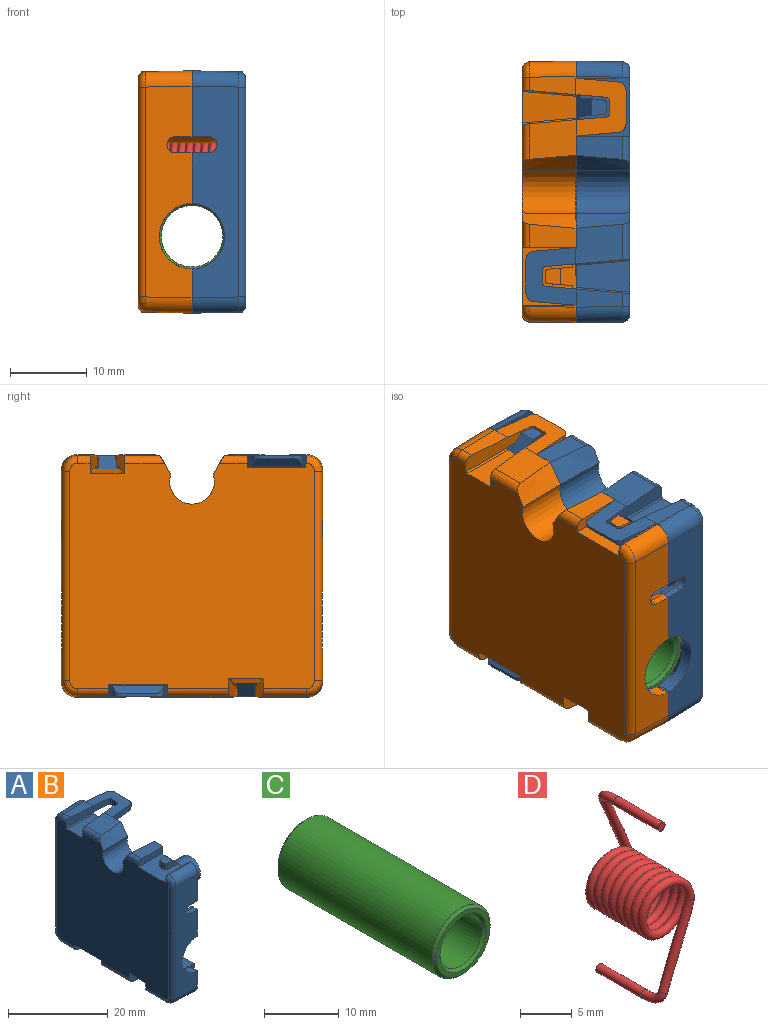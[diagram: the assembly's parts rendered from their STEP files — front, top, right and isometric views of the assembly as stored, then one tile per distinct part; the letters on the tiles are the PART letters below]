
ASSEMBLY  parts=4 mates=3
PART A: 258 faces, bbox 13.6x34.1x31.6 mm
  f0: torus R=1.84mm, axis (1,0,0), area 7.5mm2, adj f8,f153
  f1: torus R=1.85mm, axis (1,0,0), area 7.5mm2, adj f11,f71
  f2: torus R=0.75mm, axis (1,0,0), area 5.3mm2, adj f8,f70
  f3: cylinder r=4.25mm len=8.49mm, axis (0,1,0), area 22.1mm2, adj f118,f119,f120,f121,f138,f139,f140,f163
  f4: cylinder r=4.25mm len=8.49mm, axis (0,1,0), area 22.1mm2, adj f111,f113,f115,f116,f124,f136,f137,f158
  f5: cone r=2.9mm half-angle=0.5deg, axis (1,0,0), area 77.5mm2, adj f46,f125,f126,f228
  f6: torus R=2.54mm, axis (1,0,0), area 10.9mm2, adj f10,f153
  f7: cylinder r=5.7mm len=30mm, axis (0,1,0), area 113.7mm2, adj f18,f19,f20,f21,f22,f23,f24,f25
  f8: cone r=1.25mm half-angle=0.5deg, axis (-1,0,0), area 77.4mm2, adj f0,f2
  f9: cone r=2.85mm half-angle=0.5deg, axis (-1,0,0), area 191.1mm2, adj f71,f153
  f10: cone r=2mm half-angle=0.5deg, axis (-1,0,0), area 63.6mm2, adj f6,f69
  f11: cone r=1.35mm half-angle=0.5deg, axis (1,0,0), area 81.8mm2, adj f1,f52
  f12: cone r=1mm half-angle=0.5deg, axis (1,0,0), area 33.7mm2, adj f69,f170
  f13: bspline ~1.09x0.98mm, area 0.8mm2, adj f159,f171,f173,f204
  f14: bspline ~1.09x0.98mm, area 0.8mm2, adj f15,f156,f172,f219
  f15: cylinder r=1mm len=1mm, axis (0,1,0), area 1.5mm2, adj f14,f207,f219,f220
  f16: cylinder r=1mm len=1.52mm, axis (0,1,0), area 2.3mm2, adj f159,f203,f204,f206
  f17: cylinder r=1mm len=1.52mm, axis (0,1,0), area 2.3mm2, adj f156,f207,f218,f219
  f18: plane 2.5x0.33mm, normal (0.01,0,-1), area 0.8mm2, adj f7,f20,f21,f132
  f19: plane 2.5x0.33mm, normal (0.01,0,1), area 0.8mm2, adj f7,f20,f21,f132
  f20: plane 1x0.35mm, normal (0.01,-1,0), area 0.3mm2, adj f7,f18,f19,f132
  f21: plane 1x0.35mm, normal (0.01,1,0), area 0.3mm2, adj f7,f18,f19,f132
  f22: plane 1x0.35mm, normal (0.01,1,0), area 0.3mm2, adj f7,f23,f25,f134
  f23: plane 2.5x0.33mm, normal (0.01,0,-1), area 0.8mm2, adj f7,f22,f24,f134
  f24: plane 1x0.35mm, normal (0.01,-1,0), area 0.3mm2, adj f7,f23,f25,f134
  f25: plane 2.5x0.33mm, normal (0.01,0,1), area 0.8mm2, adj f7,f22,f24,f134
  f26: plane 1x0.35mm, normal (0.01,1,0), area 0.3mm2, adj f7,f27,f28,f135
  f27: plane 2.5x0.33mm, normal (0.01,0,-1), area 0.8mm2, adj f7,f26,f29,f135
  f28: plane 2.5x0.33mm, normal (0.01,0,1), area 0.8mm2, adj f7,f26,f29,f135
  f29: plane 1x0.35mm, normal (0.01,-1,0), area 0.3mm2, adj f7,f27,f28,f135
  f30: plane 3x0.2mm, normal (0.01,1,0), area 0.4mm2, adj f7,f151,f153,f167
  f31: plane 3x0.2mm, normal (0.01,-1,0), area 0.4mm2, adj f7,f152,f153,f165
  f32: plane 1x0.35mm, normal (0.01,-1,0), area 0.3mm2, adj f7,f33,f35,f133
  f33: plane 2.5x0.33mm, normal (0.01,0,1), area 0.8mm2, adj f7,f32,f34,f133
  f34: plane 1x0.35mm, normal (0.01,1,0), area 0.3mm2, adj f7,f33,f35,f133
  f35: plane 2.5x0.33mm, normal (0.01,0,-1), area 0.8mm2, adj f7,f32,f34,f133
  f36: plane 7.01x5.51mm, normal (0.01,1,0), area 21.8mm2, adj f7,f142,f150,f152,f195
  f37: plane 5.51x5.41mm, normal (0.01,-1,0), area 13.1mm2, adj f7,f142,f150,f160,f196
  f38: plane 5.51x5.51mm, normal (0.01,1,0), area 12.4mm2, adj f7,f141,f160,f221,f257
  f39: plane 5.51x5.51mm, normal (0.01,-1,0), area 12.4mm2, adj f7,f141,f167,f186,f257
  f40: plane 5.56x5.51mm, normal (0.01,1,0), area 13.9mm2, adj f7,f41,f143,f153,f223
  f41: plane 5.5x1.6mm, normal (0.01,0,1), area 8.5mm2, adj f40,f42,f153,f223
  f42: plane 5.56x5.51mm, normal (0.01,-1,0), area 13.9mm2, adj f7,f41,f143,f153,f223
  f43: plane 5.56x5.51mm, normal (0.01,-1,0), area 13.9mm2, adj f7,f44,f144,f153,f222
  f44: plane 5.5x1.6mm, normal (0.01,0,1), area 8.5mm2, adj f43,f45,f153,f222
  f45: plane 5.56x5.51mm, normal (0.01,1,0), area 13.9mm2, adj f7,f44,f144,f153,f222
  f46: plane 31.8x29.3mm, normal (-1,0,0), area 881.9mm2, adj f5,f47,f76,f77,f86,f88,f99,f100
  f47: bspline ~2x2mm, area 4mm2, adj f46,f107,f238,f239
  f48: cone r=4.2mm half-angle=1deg, axis (-1,0,0), area 30.9mm2, adj f153,f226,f228,f241
  f49: bspline ~5.58x0.64mm, area 4.3mm2, adj f50,f153,f228,f256
  f50: bspline ~5.5x0.29mm, area 1.6mm2, adj f49,f123,f153,f228
  f51: bspline ~5.5x0.29mm, area 1.6mm2, adj f123,f153,f228,f241
  f52: plane 2.52x2.52mm, normal (1,0,0), area 5mm2, adj f11
  f53: plane 4.08x3.5mm, normal (1,0,0), area 7.8mm2, adj f54,f55,f56,f57,f58,f59,f60,f61
  f54: plane 0.64x0.2mm, normal (0,0,-1), area 0.1mm2, adj f53,f55,f66,f153
  f55: plane 2.21x0.37mm, normal (0,0.99,-0.17), area 0.4mm2, adj f53,f54,f56,f153
  f56: plane 2.21x0.72mm, normal (0,-0.95,-0.31), area 0.5mm2, adj f53,f55,f57,f153
  f57: plane 0.61x0.2mm, normal (0,0,-1), area 0.1mm2, adj f53,f56,f58,f153
  f58: plane 2.21x0.73mm, normal (0,0.95,-0.31), area 0.5mm2, adj f53,f57,f59,f153
  f59: plane 2.21x0.37mm, normal (0,-0.99,-0.17), area 0.4mm2, adj f53,f58,f60,f153
  f60: plane 0.64x0.2mm, normal (0,0,-1), area 0.1mm2, adj f53,f59,f61,f153
  f61: plane 3.5x0.59mm, normal (0,0.99,0.17), area 0.7mm2, adj f53,f60,f62,f153
  f62: plane 0.65x0.2mm, normal (0,0,1), area 0.1mm2, adj f53,f61,f63,f153
  f63: plane 2.44x0.8mm, normal (0,-0.95,0.31), area 0.5mm2, adj f53,f62,f64,f153
  f64: plane 2.44x0.8mm, normal (0,0.95,0.31), area 0.5mm2, adj f53,f63,f65,f153
  f65: plane 0.65x0.2mm, normal (0,0,1), area 0.1mm2, adj f53,f64,f66,f153
  f66: plane 3.5x0.59mm, normal (0,-0.99,0.17), area 0.7mm2, adj f53,f54,f65,f153
  f67: plane 5.5x0.74mm, normal (0.01,0.8,-0.6), area 4.5mm2, adj f153,f191,f226,f228
  f68: plane 5.5x0.74mm, normal (0.01,-0.8,-0.6), area 4.5mm2, adj f153,f224,f225,f228
  f69: plane 4x4mm, normal (1,0,0), area 9.4mm2, adj f10,f12
  f70: plane 1.51x1.51mm, normal (1,0,0), area 1.8mm2, adj f2
  f71: plane 5.7x5.7mm, normal (1,0,0), area 14.8mm2, adj f1,f9
  f72: plane 5.5x0.49mm, normal (0.02,-1,0), area 2.2mm2, adj f73,f153,f173,f210
  f73: plane 5.5x1.1mm, normal (0.02,0,-1), area 5.5mm2, adj f72,f153,f155,f210
  f74: plane 5.5x0.49mm, normal (0.02,1,0), area 2.2mm2, adj f75,f153,f161,f172
  f75: plane 5.5x1.1mm, normal (0.02,0,-1), area 5.5mm2, adj f74,f153,f161,f253
  f76: plane 7x4.09mm, normal (-0.09,0,1), area 24.4mm2, adj f46,f127,f128,f251
  f77: plane 7x4.09mm, normal (-0.09,0,-1), area 24.4mm2, adj f46,f131,f243,f257
  f78: plane 2.14x1.94mm, normal (-0.02,0,-1), area 3.7mm2, adj f79,f184,f185,f229,f230,f242
  f79: plane 1.57x0.88mm, normal (-1,0,0), area 1.4mm2, adj f78,f88,f229,f230
  f80: plane 2.14x1.94mm, normal (-0.02,0,1), area 3.7mm2, adj f81,f87,f231,f232,f254,f255
  f81: plane 1.57x0.88mm, normal (-1,0,0), area 1.4mm2, adj f80,f86,f231,f232
  f82: plane 5.81x1.99mm, normal (0.09,1,0), area 9.4mm2, adj f97,f130,f160,f198,f221,f257
  f83: plane 5.81x1.99mm, normal (0.09,-1,0), area 9.4mm2, adj f84,f97,f129,f167,f186,f257
  f84: plane 5.5x4.86mm, normal (0.02,0,1), area 25.2mm2, adj f83,f85,f167,f215
  f85: cylinder r=0.5mm len=5.5mm, axis (-1,0.02,0.02), area 4.3mm2, adj f84,f167,f168,f215
  f86: plane 7.62x6.51mm, normal (-0.01,0,1), area 41.9mm2, adj f46,f81,f87,f106,f231,f232,f244,f254
  f87: plane 7.59x2.06mm, normal (0.71,0,0.71), area 10.3mm2, adj f80,f86,f106,f149,f228,f244,f245,f254
  f88: plane 7.62x6.51mm, normal (-0.01,0,-1), area 41.9mm2, adj f46,f79,f145,f148,f184,f185,f229,f230
  f89: plane 1.58x1.39mm, normal (-1,0,0), area 2.2mm2, adj f98,f103,f180,f181
  f90: plane 4.35x0.32mm, normal (1,0,0), area 1.4mm2, adj f103,f174,f175,f182
  f91: plane 1.58x1.39mm, normal (-1,0,0), area 2.2mm2, adj f97,f104,f178,f179
  f92: plane 4.35x0.32mm, normal (1,0,0), area 1.4mm2, adj f104,f176,f177,f183
  f93: plane 5.5x1.5mm, normal (0.09,1,0), area 7.9mm2, adj f97,f104,f150,f176
  f94: plane 5.5x1.5mm, normal (0.09,-1,0), area 7.9mm2, adj f97,f104,f177,f215
  f95: plane 5.5x1.5mm, normal (0.09,-1,0), area 7.9mm2, adj f98,f103,f174,f228
  f96: plane 5.5x1.5mm, normal (0.09,1,0), area 7.9mm2, adj f98,f103,f175,f252
  f97: plane 7.5x5.5mm, normal (0.01,0,1), area 25.3mm2, adj f82,f83,f91,f93,f94,f101,f102,f129
  f98: plane 7.5x5.5mm, normal (0.01,0,-1), area 25.3mm2, adj f89,f95,f96,f99,f100,f166,f180,f181
  f99: plane 10.93x2.29mm, normal (-0.09,-1,0), area 18.7mm2, adj f46,f98,f103,f128,f166,f181,f212,f235
  f100: plane 10.93x2.29mm, normal (-0.09,1,0), area 18.7mm2, adj f46,f98,f103,f108,f127,f180,f214,f250
  f101: plane 10.93x2.29mm, normal (-0.09,1,0), area 18.7mm2, adj f46,f97,f104,f129,f178,f208,f238,f243
  f102: plane 10.93x2.29mm, normal (-0.09,-1,0), area 18.7mm2, adj f46,f97,f104,f110,f130,f131,f179,f211
  f103: plane 7.51x6.51mm, normal (0.02,0,1), area 32.2mm2, adj f89,f90,f95,f96,f99,f100,f174,f175
  f104: plane 7.51x6.51mm, normal (0.02,0,-1), area 32.2mm2, adj f91,f92,f93,f94,f101,f102,f176,f177
  f105: cylinder r=2mm len=6.03mm, axis (-1,-0.02,0.02), area 18.9mm2, adj f150,f206,f213,f234
  f106: plane 6.51x1.66mm, normal (-0.01,-1,0), area 10mm2, adj f46,f86,f87,f109,f149,f227
  f107: cylinder r=2mm len=6.03mm, axis (-1,0.02,0.02), area 18.9mm2, adj f47,f207,f208,f215
  f108: cylinder r=1mm len=5.26mm, axis (0,1,0), area 7.6mm2, adj f46,f100,f126,f214
  f109: cylinder r=1mm len=3.62mm, axis (0,1,0), area 5.1mm2, adj f46,f106,f125,f227
  f110: cylinder r=1mm len=8.04mm, axis (0,1,0), area 12.4mm2, adj f46,f102,f148,f211
  f111: plane 1.28x0.48mm, normal (0.01,0,-1), area 0.6mm2, adj f4,f124,f152,f162,f165
  f112: plane 5.5x0.55mm, normal (0.01,0,1), area 2.6mm2, adj f137,f153,f155,f210
  f113: plane 3.57x0.52mm, normal (0.01,0,-1), area 1.7mm2, adj f4,f137,f153,f158
  f114: plane 5.5x0.55mm, normal (0.01,0,-1), area 2.6mm2, adj f136,f150,f152,f164
  f115: plane 1.28x0.48mm, normal (0.01,0,1), area 0.6mm2, adj f4,f124,f153,f158,f165
  f116: plane 3.57x0.52mm, normal (0.01,0,1), area 1.7mm2, adj f4,f136,f152,f162
  f117: plane 5.5x0.55mm, normal (0.01,0,-1), area 2.6mm2, adj f138,f167,f168,f215
  f118: plane 3.57x0.52mm, normal (0.01,0,1), area 1.7mm2, adj f3,f138,f163,f167
  f119: plane 1.28x0.48mm, normal (0.01,0,1), area 0.6mm2, adj f3,f139,f151,f153,f169
  f120: plane 1.28x0.48mm, normal (0.01,0,-1), area 0.6mm2, adj f3,f139,f151,f163,f167
  f121: plane 3.57x0.52mm, normal (0.01,0,-1), area 1.7mm2, adj f3,f140,f153,f169
  f122: plane 5.5x0.55mm, normal (0.01,0,1), area 2.6mm2, adj f140,f153,f161,f253
  f123: cone r=4.7mm half-angle=0.5deg, axis (-1,0,0), area 2.1mm2, adj f50,f51,f153,f228
  f124: plane 1.28x1mm, normal (0.01,-1,0), area 1.2mm2, adj f4,f111,f115,f165
  f125: bspline ~7x2.59mm, area 20.6mm2, adj f5,f46,f109,f227,f228
  f126: bspline ~7x2.59mm, area 20.6mm2, adj f5,f46,f108,f214,f228
  f127: cylinder r=0.2mm len=7.05mm, axis (-0.99,-0.09,-0.09), area 2.2mm2, adj f46,f76,f100,f250,f251
  f128: cylinder r=0.2mm len=7.05mm, axis (-0.99,0.09,-0.09), area 2.2mm2, adj f46,f76,f99,f166,f251
  f129: cylinder r=0.3mm len=1.58mm, axis (0,1,0), area 0.7mm2, adj f83,f97,f101,f243,f257
  f130: cylinder r=0.3mm len=1.58mm, axis (0,-1,0), area 0.7mm2, adj f82,f97,f102,f131,f257
  f131: cylinder r=0.2mm len=7.05mm, axis (0.99,-0.09,-0.09), area 2.2mm2, adj f46,f77,f102,f130,f257
  f132: plane 2.5x1mm, normal (1,0,0), area 2.5mm2, adj f18,f19,f20,f21
  f133: plane 2.5x1mm, normal (1,0,0), area 2.5mm2, adj f32,f33,f34,f35
  f134: plane 2.5x1mm, normal (1,0,0), area 2.5mm2, adj f22,f23,f24,f25
  f135: plane 2.5x1mm, normal (1,0,0), area 2.5mm2, adj f26,f27,f28,f29
  f136: plane 5.5x1mm, normal (0.01,-1,0), area 4.6mm2, adj f4,f114,f116,f150,f152,f202
  f137: plane 5.5x1mm, normal (0.01,-1,0), area 4.6mm2, adj f4,f112,f113,f153,f201,f210
  f138: plane 5.5x1mm, normal (0.01,1,0), area 4.6mm2, adj f3,f117,f118,f167,f215,f217
  f139: plane 1.28x1mm, normal (0.01,1,0), area 1.2mm2, adj f3,f119,f120,f151
  f140: plane 5.5x1mm, normal (0.01,1,0), area 4.6mm2, adj f3,f121,f122,f153,f161,f216
  f141: plane 2.14x1.54mm, normal (0.01,0,1), area 3.3mm2, adj f7,f38,f39,f257
  f142: plane 2.14x1.54mm, normal (0.01,0,1), area 3.3mm2, adj f7,f36,f37,f150
  f143: plane 2.14x1.54mm, normal (0.01,0,-1), area 3.3mm2, adj f7,f40,f42,f223
  f144: plane 2.14x1.54mm, normal (0.01,0,-1), area 3.3mm2, adj f7,f43,f45,f222
  f145: plane 6.51x1.66mm, normal (-0.01,-1,0), area 10mm2, adj f46,f88,f146,f213,f233,f242
  f146: plane 2.1x0.49mm, normal (0.09,-1,0), area 0.9mm2, adj f145,f150,f213,f242
  f147: plane 2.1x0.49mm, normal (0.09,1,0), area 0.9mm2, adj f148,f150,f211,f242
  f148: plane 6.51x1.66mm, normal (-0.01,1,0), area 10mm2, adj f46,f88,f110,f147,f211,f242
  f149: plane 2.1x0.49mm, normal (0.09,-1,0), area 0.9mm2, adj f87,f106,f227,f228
  f150: plane 20.89x5.77mm, normal (1,0,0), area 39.8mm2, adj f36,f37,f93,f97,f105,f114,f136,f142
  f151: plane 1x0.05mm, normal (-1,0,0), area 0.1mm2, adj f30,f119,f120,f139
  f152: plane 7.91x2.96mm, normal (1,0,0), area 20.3mm2, adj f7,f31,f36,f111,f114,f116,f136,f162
  f153: plane 30.82x19.42mm, normal (1,0,0), area 405.2mm2, adj f0,f6,f7,f9,f30,f31,f40,f41
  f154: plane 0.28x0.1mm, normal (-0.02,0,1), area 0mm2, adj f200,f209,f244,f246
  f155: plane 5.5x4.34mm, normal (0.02,-1,0), area 23.5mm2, adj f73,f112,f153,f210
  f156: plane 7.66x5.56mm, normal (0.02,1,0), area 35.1mm2, adj f14,f17,f153,f172,f193,f218,f219,f228
  f157: plane 7.24x5.5mm, normal (0.09,0,-1), area 37.3mm2, adj f153,f189,f190,f251
  f158: plane 3.59x3.31mm, normal (0.02,-1,0), area 6.6mm2, adj f4,f113,f115,f153
  f159: plane 8.76x5.56mm, normal (0.02,-1,0), area 41mm2, adj f13,f16,f153,f173,f187,f203,f204,f252
  f160: plane 15.8x6.91mm, normal (1,0,0), area 91.8mm2, adj f7,f37,f38,f82,f196,f197,f198,f221
  f161: plane 6.61x2.52mm, normal (1,0,0), area 11.4mm2, adj f74,f75,f122,f140,f172,f207,f216,f220
  f162: plane 3.59x3.31mm, normal (0.02,-1,0), area 6.6mm2, adj f4,f111,f116,f152
  f163: plane 3.59x3.31mm, normal (0.02,1,0), area 6.6mm2, adj f3,f118,f120,f167
  f164: plane 5.5x3.29mm, normal (0.02,-1,0), area 17.7mm2, adj f114,f150,f152,f194
  f165: plane 1x0.05mm, normal (-1,0,0), area 0.1mm2, adj f31,f111,f115,f124
  f166: cylinder r=0.3mm len=1.58mm, axis (0,1,0), area 0.7mm2, adj f98,f99,f128,f189,f251
  f167: plane 8.86x7.91mm, normal (1,0,0), area 53.4mm2, adj f7,f30,f39,f83,f84,f85,f117,f118
  f168: plane 5.5x3.29mm, normal (0.02,1,0), area 17.7mm2, adj f85,f117,f167,f215
  f169: plane 3.59x3.31mm, normal (0.02,1,0), area 6.6mm2, adj f3,f119,f121,f153
  f170: plane 1.9x1.9mm, normal (1,0,0), area 2.8mm2, adj f12
  f171: cylinder r=1mm len=1mm, axis (0,1,0), area 1.5mm2, adj f13,f204,f205,f206
  f172: cylinder r=1.5mm len=5.52mm, axis (-1,0.02,0.02), area 11.3mm2, adj f14,f74,f153,f156,f161,f220
  f173: cylinder r=1.5mm len=5.52mm, axis (-1,-0.02,0.02), area 11.3mm2, adj f13,f72,f153,f159,f205,f210
  f174: cylinder r=1.1mm len=1.36mm, axis (0,0,1), area 1.1mm2, adj f90,f95,f103,f182
  f175: cylinder r=1.1mm len=1.36mm, axis (0,0,-1), area 1.1mm2, adj f90,f96,f103,f182
  f176: cylinder r=1.1mm len=1.36mm, axis (0,0,-1), area 1.1mm2, adj f92,f93,f104,f183
  f177: cylinder r=1.1mm len=1.36mm, axis (0,0,1), area 1.1mm2, adj f92,f94,f104,f183
  f178: cylinder r=0.5mm len=1.4mm, axis (0,0,-1), area 1mm2, adj f91,f97,f101,f104
  f179: cylinder r=0.5mm len=1.4mm, axis (0,0,-1), area 1mm2, adj f91,f97,f102,f104
  f180: cylinder r=0.5mm len=1.4mm, axis (0,0,-1), area 1mm2, adj f89,f98,f100,f103
  f181: cylinder r=0.5mm len=1.4mm, axis (0,0,-1), area 1mm2, adj f89,f98,f99,f103
  f182: plane 6.54x1.02mm, normal (0.71,0,-0.7), area 8.6mm2, adj f90,f98,f174,f175
  f183: plane 6.54x1.02mm, normal (0.71,0,0.7), area 8.6mm2, adj f92,f97,f176,f177
  f184: plane 3.05x1.6mm, normal (-0.09,1,0), area 3.6mm2, adj f78,f88,f229,f242
  f185: plane 3.05x1.6mm, normal (-0.09,-1,0), area 3.6mm2, adj f78,f88,f230,f242
  f186: plane 5.5x4.12mm, normal (0.09,0,1), area 21.3mm2, adj f39,f83,f167,f257
  f187: cylinder r=0.5mm len=5.5mm, axis (1,0.02,0.02), area 4.3mm2, adj f153,f159,f188,f252
  f188: plane 5.5x0.86mm, normal (0.02,0,-1), area 3.2mm2, adj f153,f187,f189,f252
  f189: plane 5.81x1.99mm, normal (0.09,1,0), area 9.4mm2, adj f98,f153,f157,f166,f188,f251
  f190: plane 5.81x1.99mm, normal (0.09,-1,0), area 9.4mm2, adj f98,f153,f157,f191,f250,f251
  f191: plane 5.5x3.13mm, normal (0.02,0,-1), area 15.8mm2, adj f67,f153,f190,f228
  f192: plane 5.5x1.65mm, normal (0.01,1,0), area 8.7mm2, adj f153,f193,f224,f228
  f193: plane 9.9x5.5mm, normal (0.01,0,-1), area 54mm2, adj f153,f156,f192,f228,f247,f248,f249
  f194: cylinder r=0.5mm len=5.5mm, axis (-1,-0.02,0.02), area 4.3mm2, adj f150,f152,f164,f195
  f195: plane 5.5x2.6mm, normal (0.02,0,1), area 13.9mm2, adj f36,f150,f152,f194
  f196: plane 9.3x5.5mm, normal (0.01,0,1), area 50.9mm2, adj f37,f150,f160,f197
  f197: plane 5.5x1.65mm, normal (0.01,-1,0), area 8.7mm2, adj f150,f160,f196,f198
  f198: plane 5.51x5.5mm, normal (0.02,0,1), area 28.9mm2, adj f82,f150,f160,f197
  f199: cylinder r=2mm len=6.03mm, axis (1,0.02,0.02), area 18.9mm2, adj f206,f212,f237,f252
  f200: cylinder r=2mm len=6.03mm, axis (1,-0.02,0.02), area 18.9mm2, adj f154,f207,f209,f228,f240
  f201: plane 2x0.22mm, normal (0.05,0,-1), area 0.4mm2, adj f4,f137,f206,f210
  f202: plane 2x0.22mm, normal (0.05,0,1), area 0.4mm2, adj f4,f136,f150,f206
  f203: plane 2.27x1.54mm, normal (0.02,0,-1), area 3.4mm2, adj f16,f159,f206,f252
  f204: plane 1.5x0.09mm, normal (1,0,0), area 0.1mm2, adj f13,f16,f159,f171,f206
  f205: plane 2.27x1.04mm, normal (0.02,0,1), area 2.3mm2, adj f171,f173,f206,f210
  f206: plane 27.64x6.16mm, normal (-0.02,1,0), area 130.2mm2, adj f4,f16,f105,f150,f171,f199,f201,f202
  f207: plane 27.64x6.16mm, normal (-0.02,-1,0), area 130.2mm2, adj f3,f15,f17,f107,f161,f200,f215,f216
  f208: plane 6.37x6.02mm, normal (-0.02,0,-1), area 36.4mm2, adj f101,f104,f107,f215,f238
  f209: plane 5.74x0.25mm, normal (-0.02,0,1), area 1mm2, adj f154,f200,f228,f244,f245
  f210: plane 6.61x2.52mm, normal (1,0,0), area 11.4mm2, adj f72,f73,f112,f137,f155,f173,f201,f205
  f211: plane 8.62x6.02mm, normal (-0.02,0,-1), area 50.1mm2, adj f102,f104,f110,f147,f148,f150
  f212: plane 6.02x2.37mm, normal (-0.02,0,1), area 12.4mm2, adj f99,f103,f199,f235,f252
  f213: plane 6.02x4.25mm, normal (-0.02,0,-1), area 25.1mm2, adj f105,f145,f146,f150,f233
  f214: plane 6.02x5.15mm, normal (-0.02,0,1), area 27.8mm2, adj f100,f103,f108,f126,f228
  f215: plane 6.89x5.77mm, normal (1,0,0), area 15.2mm2, adj f84,f85,f94,f97,f107,f117,f138,f168
  f216: plane 2x0.22mm, normal (0.05,0,-1), area 0.4mm2, adj f3,f140,f161,f207
  f217: plane 2x0.22mm, normal (0.05,0,1), area 0.4mm2, adj f3,f138,f207,f215
  f218: plane 2.27x1.54mm, normal (0.02,0,-1), area 3.4mm2, adj f17,f156,f207,f228
  f219: plane 1.5x0.09mm, normal (1,0,0), area 0.1mm2, adj f14,f15,f17,f156,f207
  f220: plane 2.27x1.04mm, normal (0.02,0,1), area 2.3mm2, adj f15,f161,f172,f207
  f221: plane 5.5x1.62mm, normal (0.09,0,1), area 7.5mm2, adj f38,f82,f160,f257
  f222: plane 1.7x1.5mm, normal (1,0,0), area 2.6mm2, adj f43,f44,f45,f144
  f223: plane 1.7x1.5mm, normal (1,0,0), area 2.6mm2, adj f40,f41,f42,f143
  f224: plane 5.5x0.91mm, normal (0.02,0,-1), area 4.9mm2, adj f68,f153,f192,f228
  f225: plane 5.5x1.31mm, normal (0.02,-1,0), area 7.1mm2, adj f68,f153,f228,f256
  f226: plane 5.5x1.31mm, normal (0.02,1,0), area 7.1mm2, adj f48,f67,f153,f228
  f227: plane 6.02x3.03mm, normal (-0.02,0,1), area 16.5mm2, adj f106,f109,f125,f149,f228
  f228: plane 24.89x8.57mm, normal (1,0,0), area 52.8mm2, adj f5,f48,f49,f50,f51,f67,f68,f87
  f229: cylinder r=0.5mm len=1.57mm, axis (0,0,-1), area 1.2mm2, adj f78,f79,f88,f184
  f230: cylinder r=0.5mm len=1.57mm, axis (0,0,-1), area 1.2mm2, adj f78,f79,f88,f185
  f231: cylinder r=0.5mm len=1.57mm, axis (0,0,1), area 1.2mm2, adj f80,f81,f86,f255
  f232: cylinder r=0.5mm len=1.57mm, axis (0,0,1), area 1.2mm2, adj f80,f81,f86,f254
  f233: cylinder r=1mm len=4.09mm, axis (0,1,0), area 6.4mm2, adj f46,f145,f213,f234
  f234: bspline ~2x2mm, area 4mm2, adj f46,f105,f233,f236
  f235: cylinder r=1mm len=1.74mm, axis (0,1,0), area 2.6mm2, adj f46,f99,f212,f237
  f236: cylinder r=1mm len=27.29mm, axis (0,0,-1), area 42.4mm2, adj f46,f206,f234,f237
  f237: bspline ~2x2mm, area 4mm2, adj f46,f199,f235,f236
  f238: cylinder r=1mm len=5.74mm, axis (0,1,0), area 8.8mm2, adj f46,f47,f101,f208
  f239: cylinder r=1mm len=27.29mm, axis (0,0,-1), area 42.4mm2, adj f46,f47,f207,f240
  f240: bspline ~2x2mm, area 4mm2, adj f46,f200,f239,f246
  f241: bspline ~5.51x0.64mm, area 4.3mm2, adj f48,f51,f153,f228
  f242: plane 7.59x2.06mm, normal (0.71,0,-0.71), area 10.3mm2, adj f78,f88,f145,f146,f147,f148,f150,f184
  f243: cylinder r=0.2mm len=7.05mm, axis (0.99,0.09,-0.09), area 2.2mm2, adj f46,f77,f101,f129,f257
  f244: plane 6.51x1.66mm, normal (-0.01,1,0), area 10mm2, adj f46,f86,f87,f154,f209,f245,f246
  f245: plane 2.1x0.49mm, normal (0.09,1,0), area 0.9mm2, adj f87,f209,f228,f244
  f246: bspline ~1x0.98mm, area 0.2mm2, adj f46,f154,f240,f244
  f247: plane 0.4x0.4mm, normal (0.09,1,0), area 0.1mm2, adj f193,f228,f248
  f248: plane 0.42x0.42mm, normal (-0.7,0.06,-0.71), area 0.1mm2, adj f193,f228,f247,f249
  f249: plane 0.42x0.42mm, normal (-0.09,-1,0), area 0.1mm2, adj f193,f228,f248
  f250: cylinder r=0.3mm len=1.58mm, axis (0,-1,0), area 0.7mm2, adj f98,f100,f127,f190,f251
  f251: plane 6.28x1.21mm, normal (1,0,0), area 7.4mm2, adj f76,f127,f128,f157,f166,f189,f190,f250
  f252: plane 8.57x2.89mm, normal (1,0,0), area 13.1mm2, adj f96,f98,f159,f187,f188,f199,f203,f206
  f253: plane 5.5x4.34mm, normal (0.02,1,0), area 23.5mm2, adj f75,f122,f153,f161
  f254: plane 3.05x1.6mm, normal (-0.09,-1,0), area 3.6mm2, adj f80,f86,f87,f232
  f255: plane 3.05x1.6mm, normal (-0.09,1,0), area 3.6mm2, adj f80,f86,f87,f231
  f256: cone r=4.2mm half-angle=1deg, axis (-1,0,0), area 30.9mm2, adj f49,f153,f225,f228
  f257: plane 6.28x2.91mm, normal (1,0,0), area 10mm2, adj f38,f39,f77,f82,f83,f129,f130,f131
PART B: same geometry as A
PART C: 8 faces, bbox 11x30x11 mm
  f0: plane 10.2x10.2mm, normal (0,-1,0), area 20.9mm2, adj f6,f7
  f1: plane 10.2x10.2mm, normal (0,1,0), area 20.9mm2, adj f4,f5
  f2: cylinder r=5.5mm len=29.2mm, axis (0,1,0), area 1009.1mm2, adj f5,f7
  f3: cylinder r=4mm len=29.2mm, axis (0,1,0), area 733.9mm2, adj f4,f6
  f4: cone r=4.4mm half-angle=45deg, axis (0,1,0), area 14.9mm2, adj f1,f3
  f5: cone r=5.5mm half-angle=45deg, axis (0,-1,0), area 18.8mm2, adj f1,f2
  f6: cone r=4mm half-angle=45deg, axis (0,-1,0), area 14.9mm2, adj f0,f3
  f7: cone r=5.1mm half-angle=45deg, axis (0,1,0), area 18.8mm2, adj f0,f2
PART D: 9 faces, bbox 6.9x9x21.9 mm
  f0: bspline ~2.61x1.78mm, area 8.4mm2, adj f1,f4
  f1: bspline ~9.52x4.5mm, area 29.1mm2, adj f0,f7
  f2: bspline ~2.61x1.78mm, area 8.4mm2, adj f3,f5
  f3: bspline ~9.52x4.5mm, area 29.1mm2, adj f2,f7
  f4: cylinder r=0.47mm len=6.12mm, axis (0,-1,0), area 18.3mm2, adj f0,f8
  f5: cylinder r=0.47mm len=6.12mm, axis (0,1,0), area 18.3mm2, adj f2,f6
  f6: plane 0.95x0.95mm, normal (0,-1,0), area 0.7mm2, adj f5
  f7: bspline ~8.95x6.89mm, area 446.3mm2, adj f1,f3
  f8: plane 0.95x0.95mm, normal (0,1,0), area 0.7mm2, adj f4
PLACE A rot(axis=(0,0,1),180deg) t=(-11.35,27.74,0.75)mm
PLACE B t=(-11.35,27.74,0.75)mm
PLACE C t=(-11.35,28.32,0.75)mm
PLACE D rot(axis=(0.58,-0.58,0.58),120deg) t=(-16.6,27.73,9.7)mm
MATE fastened C.f2 <-> B.f3  axis (0,1,0) through (-11.35,42.92,0.75)mm
MATE fastened D.f4 <-> B.f153  axis (-1,0,0) through (-16.85,38.19,8.65)mm
MATE fastened A.f228 <-> B.f252  axis (-1,0,0) through (-11.35,44.74,20.25)mm
